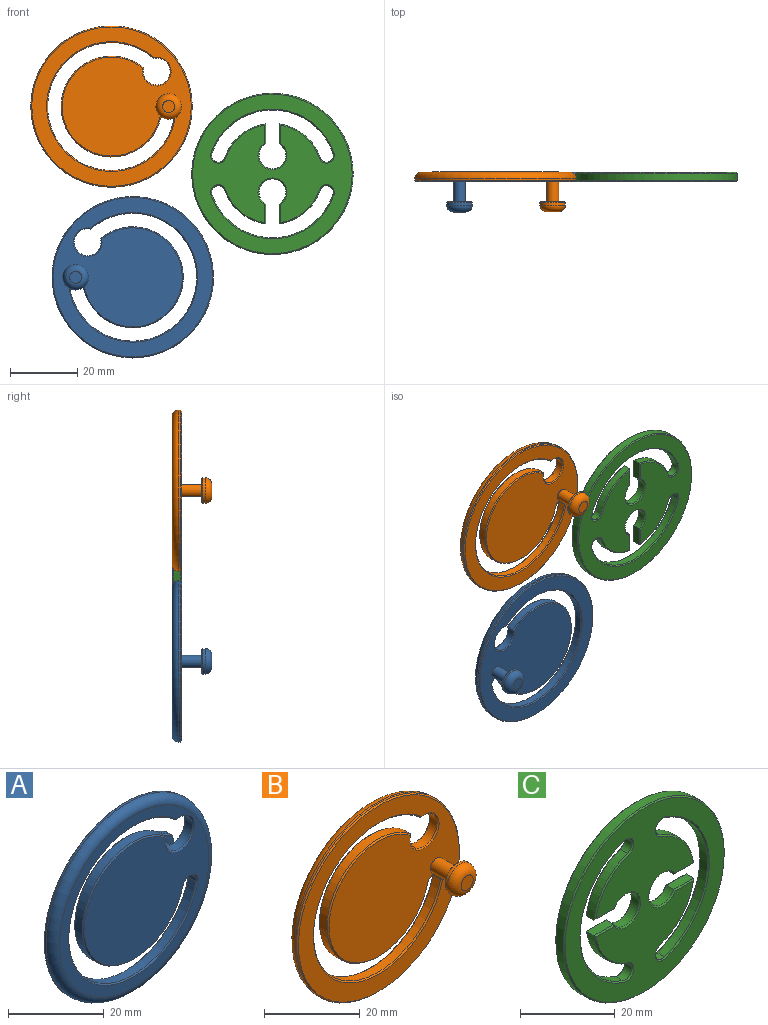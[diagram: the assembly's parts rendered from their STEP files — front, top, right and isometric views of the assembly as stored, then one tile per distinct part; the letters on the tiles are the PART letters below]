
ASSEMBLY  parts=3 mates=2
PART A: 23 faces, bbox 52x11.8x52 mm
  f0: cylinder r=2mm len=3.94mm, axis (0,-1,0), area 13.8mm2, adj f1,f3,f15,f20
  f1: cylinder r=19mm len=38mm, axis (0,-1,0), area 217.2mm2, adj f0,f2,f13,f18
  f2: cylinder r=4mm len=8mm, axis (0,-1,0), area 46mm2, adj f1,f3,f14,f17
  f3: cylinder r=15mm len=30mm, axis (0,-1,0), area 170.6mm2, adj f0,f2,f16,f19
  f4: cylinder r=24mm len=48mm, axis (0,-1,0), area 75.4mm2, adj f12,f22
  f5: plane 47.4x47.4mm, normal (0,1,0), area 1285.5mm2, adj f7,f17,f18,f19,f20,f22
  f6: plane 44x44mm, normal (0,-1,0), area 1051.6mm2, adj f12,f13,f14,f15,f16
  f7: cylinder r=1.8mm len=6.1mm, axis (0,-1,0), area 67.9mm2, adj f5,f10,f20
  f8: cylinder r=3.8mm len=7.6mm, axis (0,-1,0), area 16.7mm2, adj f11,f21
  f9: plane 3.6x3.6mm, normal (0,1,0), area 10.2mm2, adj f11
  f10: plane 7x7mm, normal (0,-1,0), area 28.3mm2, adj f7,f21
  f11: torus R=1.8mm, axis (0,1,0), area 60.7mm2, adj f8,f9
  f12: torus R=22mm, axis (0,1,0), area 459.4mm2, adj f4,f6
  f13: cone r=19.3mm half-angle=45deg, axis (0,-1,0), area 42.2mm2, adj f1,f6,f14,f15
  f14: cone r=4.3mm half-angle=45deg, axis (0,-1,0), area 9.1mm2, adj f2,f6,f13,f16
  f15: cone r=2.3mm half-angle=45deg, axis (0,-1,0), area 2.9mm2, adj f0,f6,f13,f16
  f16: cone r=15mm half-angle=45deg, axis (0,1,0), area 32.5mm2, adj f3,f6,f14,f15
  f17: cone r=4mm half-angle=45deg, axis (0,1,0), area 9.1mm2, adj f2,f5,f18,f19
  f18: cone r=19mm half-angle=45deg, axis (0,1,0), area 42.2mm2, adj f1,f5,f17,f20
  f19: cone r=14.7mm half-angle=45deg, axis (0,-1,0), area 32.5mm2, adj f3,f5,f17,f20
  f20: cone r=2mm half-angle=45deg, axis (0,1,0), area 2.8mm2, adj f0,f5,f7,f18,f19
  f21: cone r=3.8mm half-angle=45deg, axis (0,1,0), area 9.7mm2, adj f8,f10
  f22: cone r=23.7mm half-angle=45deg, axis (0,-1,0), area 63.6mm2, adj f4,f5
PART B: 23 faces, bbox 52x11.8x52 mm
  f0: cylinder r=2mm len=3.94mm, axis (0,1,0), area 13.8mm2, adj f1,f3,f15,f20
  f1: cylinder r=19mm len=38mm, axis (0,1,0), area 217.2mm2, adj f0,f2,f13,f18
  f2: cylinder r=4mm len=8mm, axis (0,1,0), area 46mm2, adj f1,f3,f14,f17
  f3: cylinder r=15mm len=30mm, axis (0,1,0), area 170.6mm2, adj f0,f2,f16,f19
  f4: cylinder r=24mm len=48mm, axis (0,1,0), area 75.4mm2, adj f12,f22
  f5: plane 47.4x47.4mm, normal (0,-1,0), area 1285.5mm2, adj f7,f17,f18,f19,f20,f22
  f6: plane 44x44mm, normal (0,1,0), area 1051.6mm2, adj f12,f13,f14,f15,f16
  f7: cylinder r=1.8mm len=6.1mm, axis (0,1,0), area 67.9mm2, adj f5,f10,f20
  f8: cylinder r=3.8mm len=7.6mm, axis (0,1,0), area 16.7mm2, adj f11,f21
  f9: plane 3.6x3.6mm, normal (0,-1,0), area 10.2mm2, adj f11
  f10: plane 7x7mm, normal (0,1,0), area 28.3mm2, adj f7,f21
  f11: torus R=1.8mm, axis (0,-1,0), area 60.7mm2, adj f8,f9
  f12: torus R=22mm, axis (0,-1,0), area 459.4mm2, adj f4,f6
  f13: cone r=19.3mm half-angle=45deg, axis (0,1,0), area 42.2mm2, adj f1,f6,f14,f15
  f14: cone r=4.3mm half-angle=45deg, axis (0,1,0), area 9.1mm2, adj f2,f6,f13,f16
  f15: cone r=2.3mm half-angle=45deg, axis (0,1,0), area 2.9mm2, adj f0,f6,f13,f16
  f16: cone r=15mm half-angle=45deg, axis (0,-1,0), area 32.5mm2, adj f3,f6,f14,f15
  f17: cone r=4mm half-angle=45deg, axis (0,-1,0), area 9.1mm2, adj f2,f5,f18,f19
  f18: cone r=19mm half-angle=45deg, axis (0,-1,0), area 42.2mm2, adj f1,f5,f17,f20
  f19: cone r=14.7mm half-angle=45deg, axis (0,1,0), area 32.5mm2, adj f3,f5,f17,f20
  f20: cone r=2mm half-angle=45deg, axis (0,-1,0), area 2.8mm2, adj f0,f5,f7,f18,f19
  f21: cone r=3.8mm half-angle=45deg, axis (0,-1,0), area 9.7mm2, adj f8,f10
  f22: cone r=23.7mm half-angle=45deg, axis (0,1,0), area 63.6mm2, adj f4,f5
PART C: 53 faces, bbox 48x2.8x48 mm
  f0: cylinder r=2mm len=3.89mm, axis (0,1,0), area 13.8mm2, adj f1,f14,f30,f47
  f1: cylinder r=19mm len=35.96mm, axis (0,1,0), area 103.8mm2, adj f0,f2,f28,f45
  f2: cylinder r=2mm len=3.89mm, axis (0,1,0), area 13.8mm2, adj f1,f3,f27,f44
  f3: cylinder r=15mm len=12.19mm, axis (0,1,0), area 36.6mm2, adj f2,f4,f29,f46
  f4: plane 5.9x2.2mm, normal (0,0,-1), area 13mm2, adj f3,f5,f31,f48
  f5: cylinder r=4mm len=8mm, axis (0,1,0), area 46.1mm2, adj f4,f6,f33,f50
  f6: plane 5.9x2.2mm, normal (0,0,1), area 13mm2, adj f5,f14,f34,f51
  f7: cylinder r=19mm len=35.96mm, axis (0,1,0), area 103.8mm2, adj f8,f15,f19,f36
  f8: cylinder r=2mm len=3.89mm, axis (0,1,0), area 13.8mm2, adj f7,f9,f20,f37
  f9: cylinder r=15mm len=12.19mm, axis (0,1,0), area 36.6mm2, adj f8,f10,f22,f39
  f10: plane 5.9x2.2mm, normal (0,0,1), area 13mm2, adj f9,f11,f24,f41
  f11: cylinder r=4mm len=8mm, axis (0,1,0), area 46.1mm2, adj f10,f12,f26,f43
  f12: plane 5.9x2.2mm, normal (0,0,-1), area 13mm2, adj f11,f13,f25,f42
  f13: cylinder r=15mm len=12.19mm, axis (0,1,0), area 36.6mm2, adj f12,f15,f23,f40
  f14: cylinder r=15mm len=12.19mm, axis (0,1,0), area 36.6mm2, adj f0,f6,f32,f49
  f15: cylinder r=2mm len=3.89mm, axis (0,1,0), area 13.8mm2, adj f7,f13,f21,f38
  f16: cylinder r=24mm len=48mm, axis (0,1,0), area 331.8mm2, adj f35,f52
  f17: plane 47.4x47.4mm, normal (0,-1,0), area 1180.4mm2, adj f36,f37,f38,f39,f40,f41,f42,f43
  f18: plane 47.4x47.4mm, normal (0,1,0), area 1180.4mm2, adj f19,f20,f21,f22,f23,f24,f25,f26
  f19: cone r=19.3mm half-angle=45deg, axis (0,1,0), area 20.2mm2, adj f7,f18,f20,f21
  f20: cone r=2.3mm half-angle=45deg, axis (0,1,0), area 2.9mm2, adj f8,f18,f19,f22
  f21: cone r=2mm half-angle=45deg, axis (0,1,0), area 2.9mm2, adj f15,f18,f19,f23
  f22: cone r=15mm half-angle=45deg, axis (0,-1,0), area 6.9mm2, adj f9,f18,f20,f24
  f23: cone r=15mm half-angle=45deg, axis (0,-1,0), area 6.9mm2, adj f13,f18,f21,f25
  f24: plane 5.91x0.3mm, normal (0,0.71,0.71), area 2.4mm2, adj f10,f18,f22,f26
  f25: plane 5.91x0.3mm, normal (0,0.71,-0.71), area 2.4mm2, adj f12,f18,f23,f26
  f26: cone r=4mm half-angle=45deg, axis (0,1,0), area 9.1mm2, adj f11,f18,f24,f25
  f27: cone r=2.3mm half-angle=45deg, axis (0,1,0), area 2.9mm2, adj f2,f18,f28,f29
  f28: cone r=19.3mm half-angle=45deg, axis (0,1,0), area 20.2mm2, adj f1,f18,f27,f30
  f29: cone r=15mm half-angle=45deg, axis (0,-1,0), area 6.9mm2, adj f3,f18,f27,f31
  f30: cone r=2mm half-angle=45deg, axis (0,1,0), area 2.9mm2, adj f0,f18,f28,f32
  f31: plane 5.91x0.3mm, normal (0,0.71,-0.71), area 2.4mm2, adj f4,f18,f29,f33
  f32: cone r=15mm half-angle=45deg, axis (0,-1,0), area 6.9mm2, adj f14,f18,f30,f34
  f33: cone r=4.3mm half-angle=45deg, axis (0,1,0), area 9.1mm2, adj f5,f18,f31,f34
  f34: plane 5.91x0.3mm, normal (0,0.71,0.71), area 2.4mm2, adj f6,f18,f32,f33
  f35: cone r=24mm half-angle=45deg, axis (0,-1,0), area 63.6mm2, adj f16,f18
  f36: cone r=19mm half-angle=45deg, axis (0,-1,0), area 20.2mm2, adj f7,f17,f37,f38
  f37: cone r=2mm half-angle=45deg, axis (0,-1,0), area 2.9mm2, adj f8,f17,f36,f39
  f38: cone r=2.3mm half-angle=45deg, axis (0,-1,0), area 2.9mm2, adj f15,f17,f36,f40
  f39: cone r=14.7mm half-angle=45deg, axis (0,1,0), area 6.9mm2, adj f9,f17,f37,f41
  f40: cone r=14.7mm half-angle=45deg, axis (0,1,0), area 6.9mm2, adj f13,f17,f38,f42
  f41: plane 5.91x0.3mm, normal (0,-0.71,0.71), area 2.4mm2, adj f10,f17,f39,f43
  f42: plane 5.91x0.3mm, normal (0,-0.71,-0.71), area 2.4mm2, adj f12,f17,f40,f43
  f43: cone r=4.3mm half-angle=45deg, axis (0,-1,0), area 9.1mm2, adj f11,f17,f41,f42
  f44: cone r=2mm half-angle=45deg, axis (0,-1,0), area 2.9mm2, adj f2,f17,f45,f46
  f45: cone r=19mm half-angle=45deg, axis (0,-1,0), area 20.2mm2, adj f1,f17,f44,f47
  f46: cone r=14.7mm half-angle=45deg, axis (0,1,0), area 6.9mm2, adj f3,f17,f44,f48
  f47: cone r=2.3mm half-angle=45deg, axis (0,-1,0), area 2.9mm2, adj f0,f17,f45,f49
  f48: plane 5.91x0.3mm, normal (0,-0.71,-0.71), area 2.4mm2, adj f4,f17,f46,f50
  f49: cone r=14.7mm half-angle=45deg, axis (0,1,0), area 6.9mm2, adj f14,f17,f47,f51
  f50: cone r=4mm half-angle=45deg, axis (0,-1,0), area 9.1mm2, adj f5,f17,f48,f51
  f51: plane 5.91x0.3mm, normal (0,-0.71,0.71), area 2.4mm2, adj f6,f17,f49,f50
  f52: cone r=23.7mm half-angle=45deg, axis (0,1,0), area 63.6mm2, adj f16,f17
PLACE A rot(axis=(0,0,-1),180deg) t=(-31.47,-22.7,-58.05)mm
PLACE B t=(-37.8,-22.3,-7.3)mm fixed
PLACE C rot(axis=(0,-1,0),90deg) t=(10.05,-22.5,-27.32)mm
MATE planar C.f1 <-> B.f5  axis (0,-1,0) through (10.05,-25.3,-27.32)mm
MATE planar B.f5 <-> A.f5  axis (0,-1,0) through (-37.6,-25.3,-7.38)mm
